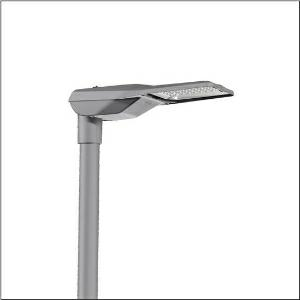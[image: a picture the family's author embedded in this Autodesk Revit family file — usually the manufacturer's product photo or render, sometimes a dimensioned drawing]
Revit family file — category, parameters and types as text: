
# Revit family: streetlight_sl_21_mini___st0_8a_5xe2c33s08gb_9548
name_source: partatom
category: Lighting Fixtures
units: mm (PartAtom-declared; Revit-internal decimal feet)

## family parameters
Cut with Voids When Loaded = No
Host = Face
Light Source = No
Part Type = Normal
Room Calculation Point = No
Round Connector Dimension = Use Diameter
Shared = No

## types (1)
- --- (1 x LED, 5940 lm, 40.4 W, 3000K)
    Apparent Load = 40 VA
    CIE Flux Codes = 38 75 97 100 100
    Color Rendering = 70
    Color Temperature = 3000K
    Default Elevation = 1800 mm
    Description = Streetlight SL 21 mini, mast luminaire, primary light control with lens, of PMMA, primary optical cover: cover, of toughened safety glass, transparent, light distribution: ST0.8a, light emission: direct distribution, primary light characteristic: asymmetric, installation type: side-entry, post-top, LED, High Power LED, rated luminous flux: 5.940lm, luminous efficacy: 147lm/W, light colour: 730, colour temperature: 3000K, control gear: D4i, control: overheat protection, constant luminous flux control, time-dependent luminous flux control, flexible luminous flux parameterisation, pre-setting: logarithmic dimming characteristic, mains connection: 220..240V, AC, 50/60Hz, start of lifetime: 40W, end of service life: 41W, reduction: 19W, luminaire housing, of diecast aluminium, powder-coated, Siteco® metallic grey (DB 702S), corrosivity category C5 mid according to DIN EN ISO 12944, please order mast flange separately, inclination adjustable: 0°, 5°, 10°, 15°, sealing non-destructively replaceable, multi-level sealing system, length: 628mm, width: 235mm, height: 110mm, mast flange for spigot size: 42mm (side-entry): 5XC10008XM4, 60/48mm (side-entry/post-top): 5XC10108XM2, 76/60mm (side-entry/post-top): 5XC10108XM1, mounting height: 4..8m, Smart Interface above, protection rating (complete): IP66, insulation class (complete): insulation class II (safety insulation), certification: CE, ENEC, ENEC+, VDE, impact resistance: IK10, permissible operating ambient temperature for outdoor applications: -40..+50°C, standard-compliant lighting for roads and squares, packaging unit: 1 piece

Light Distribution: ST0.8a
    Height = 110 mm
    Lamp = 1 x LED
    Lamp Light Flux = 5940 lm
    Lamp Power = 40.4 W
    Lamp count = 1
    Length = 625 mm
    Luminous efficacy = 147 lm/W
    Manufacturer = Siteco
    ModVariant = No
    Model = 5XE2C33S08GB
    Number of Poles = 1
    OnlyDefault = Yes
    Power Factor = 1
    Product Name = Streetlight SL 21 mini | ST0.8a
    Product group = mast luminaire | pylon top
    ProductGroupID = 6100
    Protection Class = Protection class II
    Protection Degree = IP 66
    RLX_Detail_Level = 1
    RLX_Emergency_Light_Flux = 0 lm
    RLX_Emergency_Type = 0
    RLX_Emergency_Type_DB = No
    RlxData = <blob elided: 26221 chars, md5=a43b120e>
    Socket = socket
    Standby Power = 0 W
    System Light Flux = 5940 lm
    System Power = 40 W
    Type Comments = factory setting: luminous flux: 100 % | dim-lin: 254 | 812 mA
    Type Image = l_1003515.jpg
    URL = http://relux.com
    VarID = @adj_185564
    Voltage = 0 V
    Weight = 0.00 kg
    Width = 234 mm

## geometry (parser evidence)
native form markers: Blend x4, Sweep x13
no freeform markers — native parametric forms only
